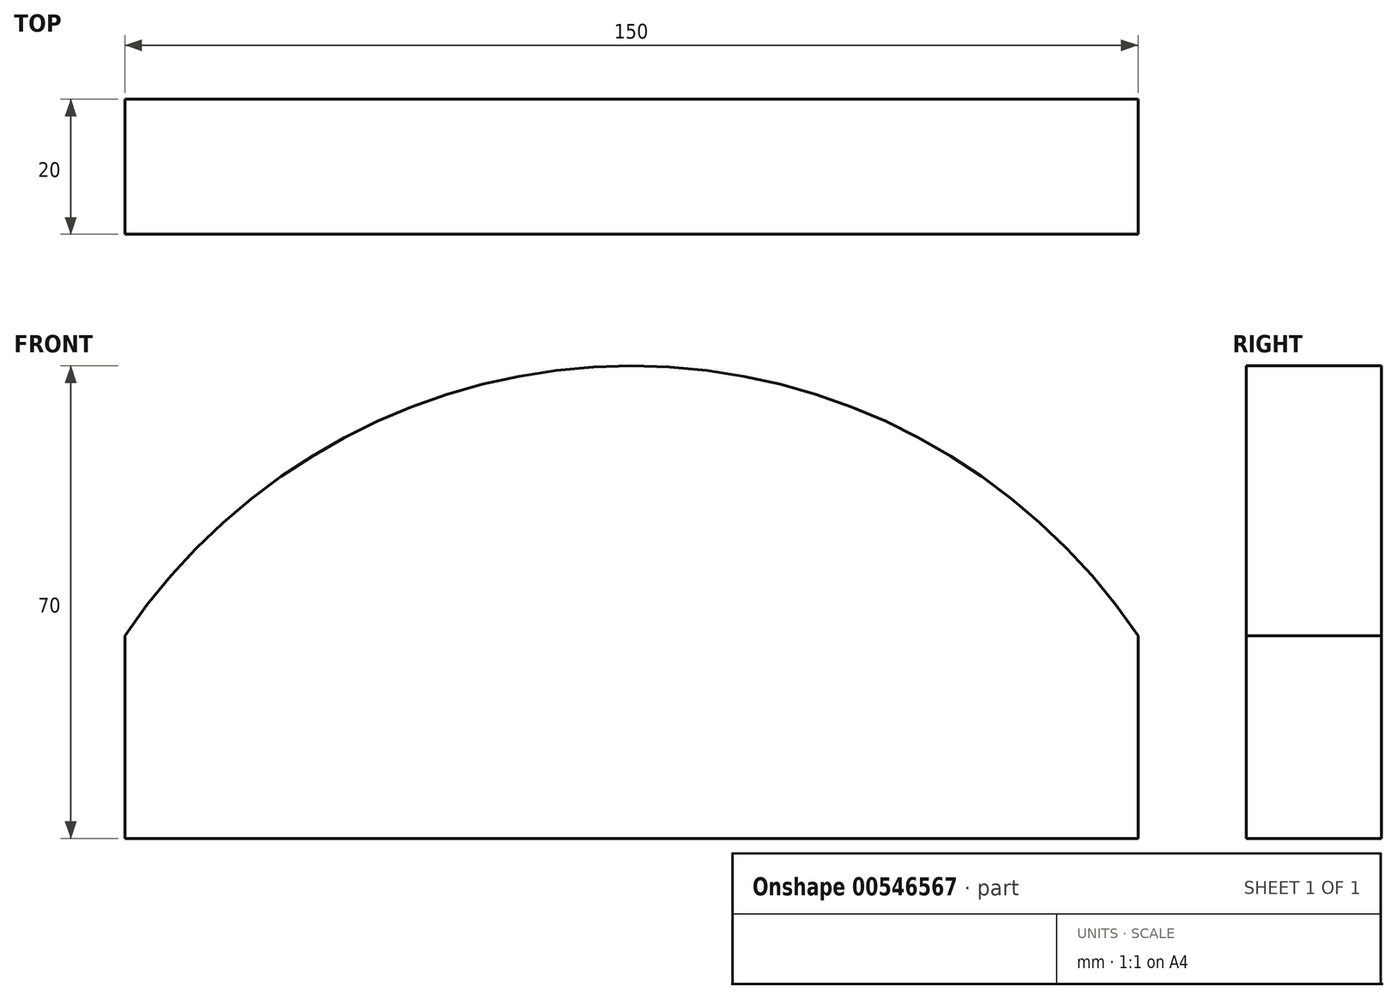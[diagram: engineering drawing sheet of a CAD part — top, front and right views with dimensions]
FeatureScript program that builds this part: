
annotation { "Feature Type Name" : "Feature", "Feature Type Description" : "" }
export const myFeature = defineFeature(function(context is Context, id is Id, definition is map)
    precondition{}
    {
        {
            var Q0;
            Q0=qCreatedBy(makeId("Front.planeOp"),FACE);
            var sketch = newSketch(context, id + "F0", { "sketchPlane" : qUnion([Q0])});
            skLineSegment(sketch, "E0", {"start": v(-65.28, 29.73) * mm, "end": v(-65.28, -0.27) * mm});
            skLineSegment(sketch, "E1", {"start": v(-65.28, -0.27) * mm, "end": v(84.72, -0.27) * mm});
            skLineSegment(sketch, "E2", {"start": v(84.72, -0.27) * mm, "end": v(84.72, 29.73) * mm});
            skArc(sketch, "E3", {"start": v(84.72, 29.73) * mm, "mid": v(9.72, 69.73) * mm, "end": v(-65.28, 29.73) * mm});
            skSolve(sketch);
        }
        {
            var Q0;
            Q0=makeQuery(id+"F0.imprint","IMPRINT",FACE,{"disambiguationData":[TD([[makeQuery(id+"F0.imprint","IMPRINT",EDGE,{"derivedFrom":sQuery(id+"F0.wireOp",EDGE,"bnv2EGET-6i3T-vAvH-e7dr-hGzWCPSLtMQ2.top")}),1.0]])]});
            var Q1;
            Q1=makeQuery(id+"F0.imprint","IMPRINT",FACE,{"disambiguationData":[TD([[makeQuery(id+"F0.imprint","IMPRINT",EDGE,{"derivedFrom":sQuery(id+"F0.wireOp",EDGE,"E0")}),1.0]])]});
            extrude(context, id + "F1", {"entities" : qUnion([Q0, Q1]), "depth" : 20 * mm, "offsetDistance" : 25 * mm});
        }
    });
